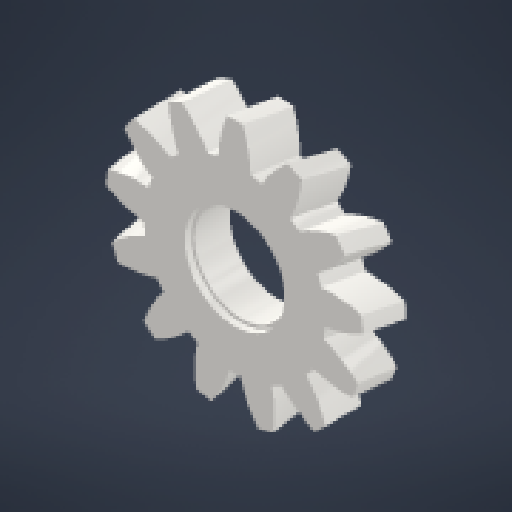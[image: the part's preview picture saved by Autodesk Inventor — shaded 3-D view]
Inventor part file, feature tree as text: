
AUTODESK INVENTOR PART (.ipt)
format: ipt  version: 2024.2 (Build 282272000, 272)  size: 386,560 bytes
history: native  units: in
note: dims shown in document units (in); Inventor stores cm internally (conversion verified against a paired STEP export)
features: other x12, plane x3, sketch x2
ambient origin geometry x8: Origin, YZ Plane, XZ Plane, XY Plane, X Axis, Y Axis, Z Axis, Center Point
bodies: Solid1 (feature_tree)
feature tree (17):
  other  "Spur Gear1"
  other  "Solid1::Spur Gear1"
  other  "TaggingFeature1"
  sketch  "Sketch1"  dims[d0=0.3937in]
  sketch  "Sketch2"  dims[d9=0.0in d14=0.0in d15=1.3982in d16=0.0in d17=0.0in d18=0.0in d19=1.3982in]
  plane  "XZ Plane_1"
  plane  "Work Plane2"
  plane  "Work Plane3"
  other  "Srf1"
  other  "Srf1::Derived"
  other  "Start plane iMate"
  other  "Distance iMate"
  other  "Position iMate"
  other  "Mesh iMate"
  other  "Axis iMate"
  other  "Mesh iMate2"
  other  "Align iMate"
